# Revit family: Shower-Valve_Trim-KOHLER-Singulier-K-10880IN
name_source: partatom
category: Specialty Equipment
revit_build: Autodesk Revit 2017 (Build: 20160225_1515(x64)
units: mm (PartAtom-declared; Revit-internal decimal feet)

## family parameters
Cut with Voids When Loaded = No
Host = Face
OmniClass Number = 23.31.25.00
OmniClass Title = Toilet and Bath Specialties
Part Type = Normal
Room Calculation Point = No
Round Connector Dimension = Use Diameter
Shared = No

## types (3) — shared parameters
ADA Compliant = No
Assembly Code = C1030200
Date Modified = 03/12/2021
Default Elevation = 42"
Description = Shower Only Trim
Height = 6 11/16"
Length = 2 5/8"
Manufacturer = KOHLER Co.
Master Format 2014 = 10 28 00
Master Format 2014 Name = Toilet, Bath, and Laundry Accessories
Material = Primium metal construction
Product Name = Singulier
URL = https://www.kohler.co.in
WaterSense Certified = No
Width = 4 9/16"

## per-type parameters (varying)
| type | Finish | Model | Product Page URL | Type |
| AF- French Gold | Kohler-Metal-AF-Vibrant_French_Gold | K-10880IN-4-AF | https://www.kohler.co.in | 1 |
| 4FP, CP- Polished Chrome | Kohler-Metal-CP-Polished_Chrome | K-10880IN-4FP-CP |  | 2 |
| 4FP, AF- French Gold | Kohler-Metal-AF-Vibrant_French_Gold | K-10880IN-4FP-AF |  | 3 |

## geometry (parser evidence)
native form markers: Sweep x6
no freeform markers — native parametric forms only
